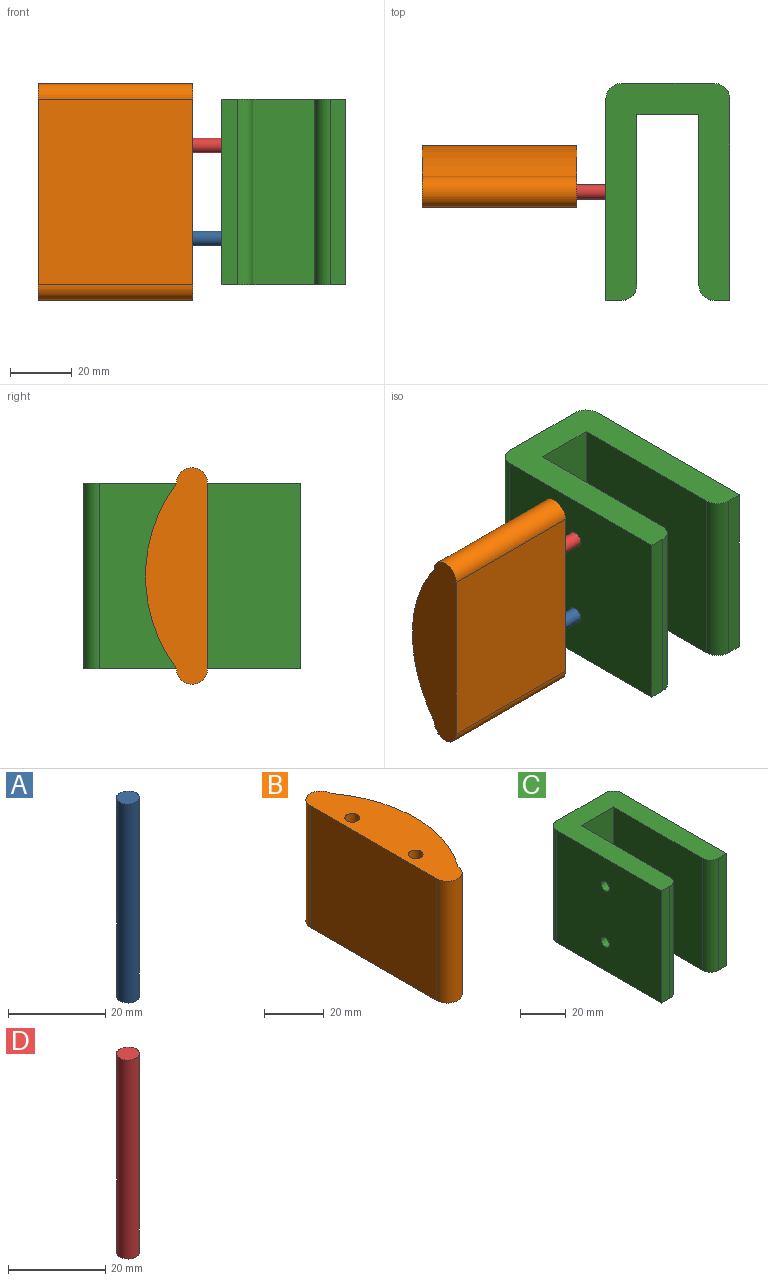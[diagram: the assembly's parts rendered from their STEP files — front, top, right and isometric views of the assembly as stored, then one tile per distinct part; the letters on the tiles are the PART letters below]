
ASSEMBLY  parts=4 mates=3
PART A: 3 faces, bbox 4.7x4.7x50 mm
  f0: cylinder r=2.35mm len=50mm, axis (0,0,-1), area 738.3mm2, adj f1,f2
  f1: plane 4.7x4.7mm, normal (0,0,1), area 17.3mm2, adj f0
  f2: plane 4.7x4.7mm, normal (0,0,-1), area 17.3mm2, adj f0
PART B: 10 faces, bbox 20x70x50 mm
  f0: cylinder r=5mm len=50mm, axis (0,0,-1), area 785.4mm2, adj f1,f4,f6,f7
  f1: plane 60x50mm, normal (-1,0,0), area 3000mm2, adj f0,f2,f6,f7
  f2: cylinder r=5mm len=50mm, axis (0,0,-1), area 785.4mm2, adj f1,f4,f6,f7
  f3: cylinder r=2.5mm len=41mm, axis (0,0,-1), area 644mm2, adj f6,f9
  f4: cylinder r=50mm len=60mm, axis (0,0,-1), area 3217.5mm2, adj f0,f2,f6,f7
  f5: cylinder r=2.5mm len=41mm, axis (0,0,-1), area 644mm2, adj f6,f8
  f6: plane 70x20mm, normal (0,0,1), area 1048mm2, adj f0,f1,f2,f3,f4,f5
  f7: plane 70x20mm, normal (0,0,-1), area 1087.3mm2, adj f0,f1,f2,f4
  f8: plane 5x5mm, normal (0,0,1), area 19.6mm2, adj f5
  f9: plane 5x5mm, normal (0,0,1), area 19.6mm2, adj f3
PART C: 18 faces, bbox 40x70x60 mm
  f0: plane 60x30mm, normal (0,1,0), area 1800mm2, adj f8,f9,f14,f17
  f1: plane 65x60mm, normal (-1,0,0), area 3860.7mm2, adj f2,f8,f9,f10,f12,f14
  f2: plane 60x5mm, normal (0,-1,0), area 300mm2, adj f1,f8,f9,f15
  f3: plane 60x55mm, normal (1,0,0), area 3300mm2, adj f4,f8,f9,f15
  f4: plane 60x20mm, normal (0,-1,0), area 1200mm2, adj f3,f5,f8,f9
  f5: plane 60x55mm, normal (-1,0,0), area 3300mm2, adj f4,f8,f9,f16
  f6: plane 60x5mm, normal (0,-1,0), area 300mm2, adj f7,f8,f9,f16
  f7: plane 65x60mm, normal (1,0,0), area 3900mm2, adj f6,f8,f9,f17
  f8: plane 70x40mm, normal (0,0,1), area 1578.5mm2, adj f0,f1,f2,f3,f4,f5,f6,f7
  f9: plane 70x40mm, normal (0,0,-1), area 1578.5mm2, adj f0,f1,f2,f3,f4,f5,f6,f7
  f10: cylinder r=2.5mm len=8mm, axis (-1,0,0), area 125.7mm2, adj f1,f11
  f11: plane 5x5mm, normal (-1,0,0), area 19.6mm2, adj f10
  f12: cylinder r=2.5mm len=8mm, axis (-1,0,0), area 125.7mm2, adj f1,f13
  f13: plane 5x5mm, normal (-1,0,0), area 19.6mm2, adj f12
  f14: cylinder r=5mm len=60mm, axis (0,0,1), area 471.2mm2, adj f0,f1,f8,f9
  f15: cylinder r=5mm len=60mm, axis (0,0,-1), area 471.2mm2, adj f2,f3,f8,f9
  f16: cylinder r=5mm len=60mm, axis (0,0,-1), area 471.2mm2, adj f5,f6,f8,f9
  f17: cylinder r=5mm len=60mm, axis (0,0,-1), area 471.2mm2, adj f0,f7,f8,f9
PART D: 3 faces, bbox 4.7x4.7x50 mm
  f0: cylinder r=2.35mm len=50mm, axis (0,0,-1), area 738.3mm2, adj f1,f2
  f1: plane 4.7x4.7mm, normal (0,0,1), area 17.3mm2, adj f0
  f2: plane 4.7x4.7mm, normal (0,0,-1), area 17.3mm2, adj f0
PLACE A rot(axis=(0.71,0,-0.71),180deg) t=(-41.28,69.36,-48.23)mm
PLACE B rot(axis=(0.58,0.58,0.58),120deg) t=(-109.24,-18.42,-4.16)mm
PLACE C t=(-4.16,19.73,-24)mm
PLACE D rot(axis=(-0.71,0,-0.71),180deg) t=(-90.86,69.23,69.58)mm
MATE slider D.f0 <-> C.f10  axis (1,0,0) through (-40.86,16.42,21)mm
MATE slider B.f3 <-> A.f0  axis (-1,0,0) through (-59.24,16.42,-9)mm
MATE slider A.f0 <-> C.f12  axis (1,0,0) through (-41.28,16.42,-9)mm
